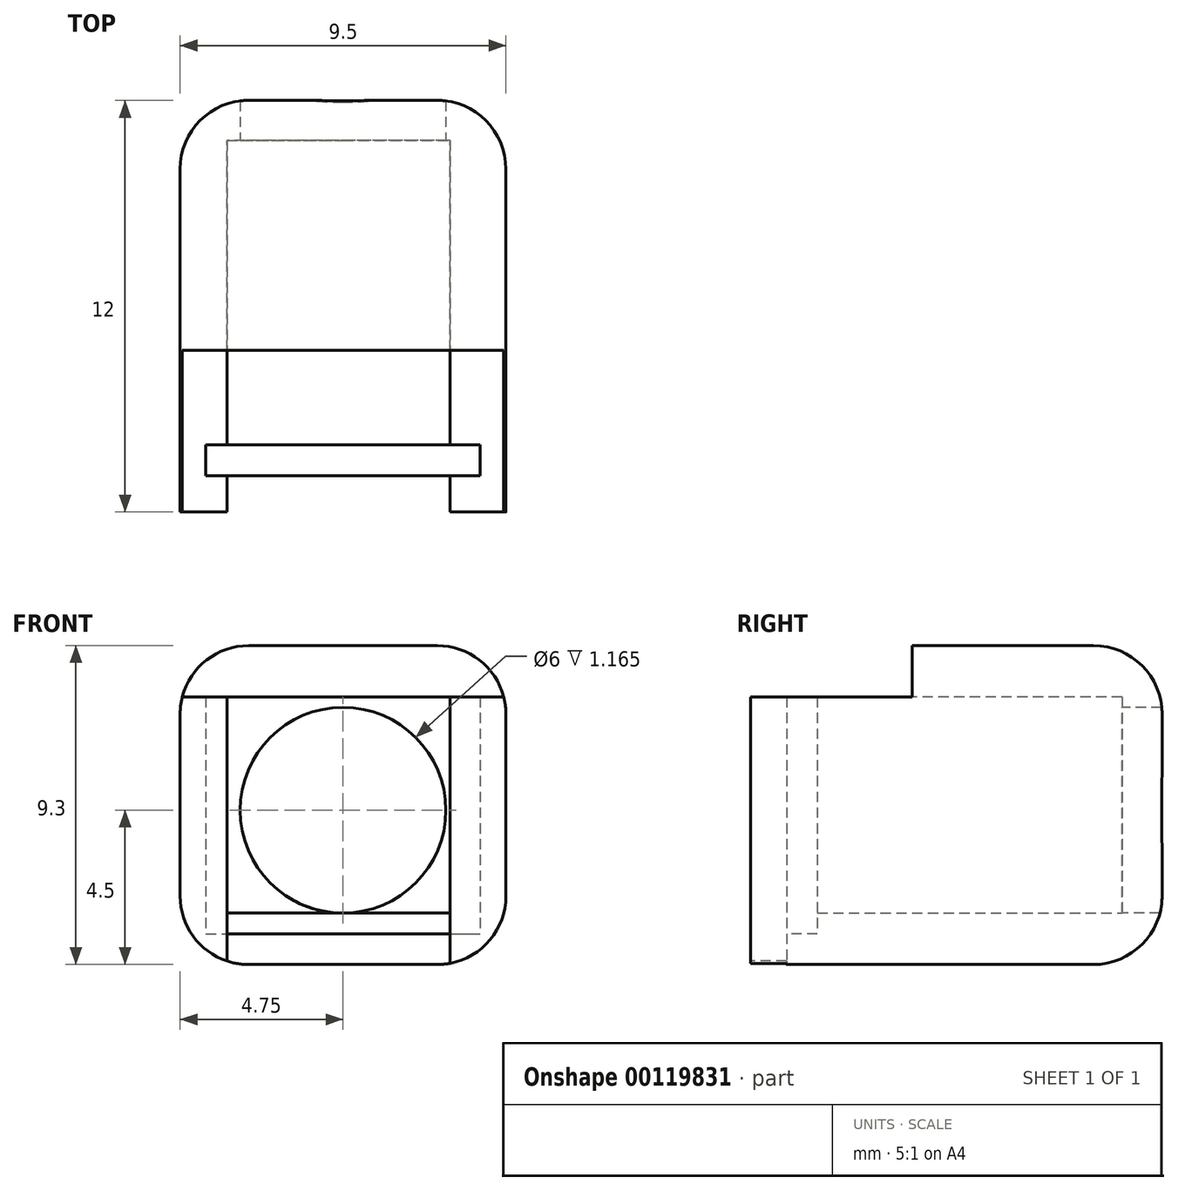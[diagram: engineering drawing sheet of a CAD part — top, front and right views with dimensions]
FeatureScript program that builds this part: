
annotation { "Feature Type Name" : "Feature", "Feature Type Description" : "" }
export const myFeature = defineFeature(function(context is Context, id is Id, definition is map)
    precondition{}
    {
        {
            var Q0;
            Q0=qCreatedBy(makeId("Top.planeOp"),FACE);
            var sketch = newSketch(context, id + "F0", { "sketchPlane" : qUnion([Q0])});
            skPoint(sketch, "E0.rect.middle", {"position": v(0, 0) * mm});
            skLineSegment(sketch, "E1.rect.bottom", {"start": v(-4.75, -1.5) * mm, "end": v(4.75, -1.5) * mm});
            skLineSegment(sketch, "E1.rect.top", {"start": v(-4.75, 1.5) * mm, "end": v(-3.38, 1.5) * mm});
            skLineSegment(sketch, "E1.rect.left", {"start": v(-4.75, -1.5) * mm, "end": v(-4.75, 1.5) * mm});
            skLineSegment(sketch, "E1.rect.right", {"start": v(4.75, -1.5) * mm, "end": v(4.75, 1.5) * mm});
            skLineSegment(sketch, "E2.rect.bottom", {"start": v(4, -0.45) * mm, "end": v(-4, -0.45) * mm});
            skLineSegment(sketch, "E2.rect.top", {"start": v(4, 0.45) * mm, "end": v(-4, 0.45) * mm});
            skLineSegment(sketch, "E2.rect.left", {"start": v(4, -0.45) * mm, "end": v(4, 0.45) * mm});
            skLineSegment(sketch, "E2.rect.right", {"start": v(-4, -0.45) * mm, "end": v(-4, 0.45) * mm});
            skLineSegment(sketch, "E3.rect.bottom", {"start": v(-3.12, -1.5) * mm, "end": v(3.38, -1.5) * mm});
            skLineSegment(sketch, "E4.trimOffspring", {"start": v(3.12, 1.5) * mm, "end": v(4.75, 1.5) * mm});
            skLineSegment(sketch, "E5", {"start": v(-3.38, 1.5) * mm, "end": v(3.12, 1.5) * mm, "construction": true});
            skLineSegment(sketch, "E6.bottom", {"start": v(4.75, 1.5) * mm, "end": v(-4.75, 1.5) * mm});
            skLineSegment(sketch, "E7.bottom", {"start": v(3.12, 1.5) * mm, "end": v(-4.75, 1.5) * mm});
            skLineSegment(sketch, "E8.bottom", {"start": v(-4.75, 1.5) * mm, "end": v(4.75, 1.5) * mm});
            skLineSegment(sketch, "E8.top", {"start": v(-4.75, 10.5) * mm, "end": v(4.75, 10.5) * mm});
            skLineSegment(sketch, "E8.left", {"start": v(-4.75, 1.5) * mm, "end": v(-4.75, 10.5) * mm});
            skLineSegment(sketch, "E8.right", {"start": v(4.75, 1.5) * mm, "end": v(4.75, 10.5) * mm});
            skLineSegment(sketch, "E9", {"start": v(-3.38, 1.5) * mm, "end": v(-3.38, 10.5) * mm});
            skLineSegment(sketch, "E10", {"start": v(3.12, 1.5) * mm, "end": v(3.12, 10.5) * mm});
            skLineSegment(sketch, "E11", {"start": v(4.75, 9.33) * mm, "end": v(-4.75, 9.33) * mm});
            skLineSegment(sketch, "E12", {"start": v(-3.38, 1.5) * mm, "end": v(-3.38, -1.5) * mm});
            skLineSegment(sketch, "E13", {"start": v(3.12, 1.5) * mm, "end": v(3.12, -1.5) * mm});
            skSolve(sketch);
        }
        {
            var Q0;
            {var subQ0=sQuery(id+"F0.wireOp",EDGE,"E6.right");Q0=makeQuery(id+"F0.imprint","IMPRINT",FACE,{"disambiguationData":[TD([[makeQuery(id+"F0.imprint","IMPRINT",EDGE,{"derivedFrom":subQ0}),-1.0]])]});}
            var Q1;
            Q1=makeQuery(id+"F0.imprint","IMPRINT",FACE,{"disambiguationData":[TD([[makeQuery(id+"F0.imprint","IMPRINT",EDGE,{"derivedFrom":sQuery(id+"F0.wireOp",EDGE,"E7.bottom")}),-1.0]])]});
            var Q2;
            {var subQ5=sQuery(id+"F0.wireOp",EDGE,"E7.bottom");Q2=makeQuery(id+"F0.imprint","IMPRINT",FACE,{"disambiguationData":[TD([[makeQuery(id+"F0.imprint","IMPRINT",EDGE,{"derivedFrom":subQ5}),1.0]])]});}
            var Q3;
            {var subQ8=sQuery(id+"F0.wireOp",EDGE,"E1.rect.right");Q3=makeQuery(id+"F0.imprint","IMPRINT",FACE,{"disambiguationData":[TD([[makeQuery(id+"F0.imprint","IMPRINT",EDGE,{"derivedFrom":subQ8}),1.0]])]});}
            var Q4;
            {var subQ5=sQuery(id+"F0.wireOp",EDGE,"E3.rect.bottom");Q4=makeQuery(id+"F0.imprint","IMPRINT",FACE,{"disambiguationData":[TD([[makeQuery(id+"F0.imprint","IMPRINT",EDGE,{"derivedFrom":subQ5}),1.0]])]});}
            var Q5;
            {var subQ4=sQuery(id+"F0.wireOp",EDGE,"E1.rect.left");Q5=makeQuery(id+"F0.imprint","IMPRINT",FACE,{"disambiguationData":[TD([[makeQuery(id+"F0.imprint","IMPRINT",EDGE,{"derivedFrom":subQ4}),-1.0]])]});}
            var Q6;
            {var subQ0=sQuery(id+"F0.wireOp",EDGE,"E6.left");Q6=makeQuery(id+"F0.imprint","IMPRINT",FACE,{"disambiguationData":[TD([[makeQuery(id+"F0.imprint","IMPRINT",EDGE,{"derivedFrom":subQ0}),1.0]])]});}
            var Q7;
            {var subQ0=sQuery(id+"F0.wireOp",EDGE,"E3.rect.right");var subQ1=sQuery(id+"F0.wireOp",EDGE,"E2.rect.bottom");var subQ2=makeQuery(id+"F0.imprint","INTERSECT",VERTEX,{"derivedFrom":[subQ1,subQ0]});Q7=makeQuery(id+"F0.imprint","IMPRINT",FACE,{"disambiguationData":[TD([[makeQuery(id+"F0.imprint","IMPRINT",EDGE,{"disambiguationData":[TD([[subQ2,-1.0]])],"derivedFrom":subQ1}),-1.0]])]});}
            var Q8;
            {var subQ0=sQuery(id+"F0.wireOp",EDGE,"E2.rect.right");Q8=makeQuery(id+"F0.imprint","IMPRINT",FACE,{"disambiguationData":[TD([[makeQuery(id+"F0.imprint","IMPRINT",EDGE,{"derivedFrom":subQ0}),-1.0]])]});}
            var Q9;
            {var subQ0=sQuery(id+"F0.wireOp",EDGE,"E2.rect.left");Q9=makeQuery(id+"F0.imprint","IMPRINT",FACE,{"disambiguationData":[TD([[makeQuery(id+"F0.imprint","IMPRINT",EDGE,{"derivedFrom":subQ0}),1.0]])]});}
            var Q10;
            {var subQ0=sQuery(id+"F0.wireOp",EDGE,"E8.left");var subQ5=sQuery(id+"F0.wireOp",EDGE,"E11");var subQ6=makeQuery(id+"F0.imprint","INTERSECT",VERTEX,{"derivedFrom":[subQ0,subQ5]});Q10=makeQuery(id+"F0.imprint","IMPRINT",FACE,{"disambiguationData":[TD([[makeQuery(id+"F0.imprint","IMPRINT",EDGE,{"disambiguationData":[TD([[subQ6,1.0]])],"derivedFrom":subQ5}),1.0]])]});}
            var Q11;
            {var subQ0=sQuery(id+"F0.wireOp",EDGE,"E8.left");var subQ1=sQuery(id+"F0.wireOp",EDGE,"E8.top");var subQ2=makeQuery(id+"F0.imprint","INTERSECT",VERTEX,{"derivedFrom":[subQ1,subQ0]});Q11=makeQuery(id+"F0.imprint","IMPRINT",FACE,{"disambiguationData":[TD([[makeQuery(id+"F0.imprint","IMPRINT",EDGE,{"disambiguationData":[TD([[subQ2,-1.0]])],"derivedFrom":subQ1}),-1.0]])]});}
            var Q12;
            {var subQ0=sQuery(id+"F0.wireOp",EDGE,"E9");var subQ1=sQuery(id+"F0.wireOp",EDGE,"E8.top");var subQ2=makeQuery(id+"F0.imprint","INTERSECT",VERTEX,{"derivedFrom":[subQ1,subQ0]});Q12=makeQuery(id+"F0.imprint","IMPRINT",FACE,{"disambiguationData":[TD([[makeQuery(id+"F0.imprint","IMPRINT",EDGE,{"disambiguationData":[TD([[subQ2,-1.0]])],"derivedFrom":subQ1}),-1.0]])]});}
            var Q13;
            {var subQ0=sQuery(id+"F0.wireOp",EDGE,"E8.right");var subQ1=sQuery(id+"F0.wireOp",EDGE,"E8.top");var subQ2=makeQuery(id+"F0.imprint","INTERSECT",VERTEX,{"derivedFrom":[subQ1,subQ0]});Q13=makeQuery(id+"F0.imprint","IMPRINT",FACE,{"disambiguationData":[TD([[makeQuery(id+"F0.imprint","IMPRINT",EDGE,{"disambiguationData":[TD([[subQ2,1.0]])],"derivedFrom":subQ1}),-1.0]])]});}
            var Q14;
            {var subQ0=sQuery(id+"F0.wireOp",EDGE,"E8.right");var subQ5=sQuery(id+"F0.wireOp",EDGE,"E11");var subQ6=makeQuery(id+"F0.imprint","INTERSECT",VERTEX,{"derivedFrom":[subQ0,subQ5]});Q14=makeQuery(id+"F0.imprint","IMPRINT",FACE,{"disambiguationData":[TD([[makeQuery(id+"F0.imprint","IMPRINT",EDGE,{"disambiguationData":[TD([[subQ6,-1.0]])],"derivedFrom":subQ5}),1.0]])]});}
            var Q15;
            {var subQ0=sQuery(id+"F0.wireOp",EDGE,"E3.rect.right");var subQ1=sQuery(id+"F0.wireOp",EDGE,"E2.rect.top");var subQ2=makeQuery(id+"F0.imprint","INTERSECT",VERTEX,{"derivedFrom":[subQ1,subQ0]});Q15=makeQuery(id+"F0.imprint","IMPRINT",FACE,{"disambiguationData":[TD([[makeQuery(id+"F0.imprint","IMPRINT",EDGE,{"disambiguationData":[TD([[subQ2,-1.0]])],"derivedFrom":subQ1}),-1.0]])]});}
            var Q16;
            {var subQ0=sQuery(id+"F0.wireOp",EDGE,"E9");var subQ5=sQuery(id+"F0.wireOp",EDGE,"E11");var subQ6=makeQuery(id+"F0.imprint","INTERSECT",VERTEX,{"derivedFrom":[subQ0,subQ5]});Q16=makeQuery(id+"F0.imprint","IMPRINT",FACE,{"disambiguationData":[TD([[makeQuery(id+"F0.imprint","IMPRINT",EDGE,{"disambiguationData":[TD([[subQ6,1.0]])],"derivedFrom":subQ5}),1.0]])]});}
            extrude(context, id + "F1", {"entities" : qUnion([Q0, Q1, Q2, Q3, Q4, Q5, Q6, Q7, Q8, Q9, Q10, Q11, Q12, Q13, Q14, Q15, Q16]), "depth" : 0.9 * mm});
        }
        {
            var Q0;
            {var subQ0=sQuery(id+"F0.wireOp",EDGE,"E6.left");Q0=makeQuery(id+"F0.imprint","IMPRINT",FACE,{"disambiguationData":[TD([[makeQuery(id+"F0.imprint","IMPRINT",EDGE,{"derivedFrom":subQ0}),1.0]])]});}
            var Q1;
            {var subQ0=sQuery(id+"F0.wireOp",EDGE,"E6.right");Q1=makeQuery(id+"F0.imprint","IMPRINT",FACE,{"disambiguationData":[TD([[makeQuery(id+"F0.imprint","IMPRINT",EDGE,{"derivedFrom":subQ0}),-1.0]])]});}
            var Q2;
            {var subQ5=sQuery(id+"F0.wireOp",EDGE,"E3.rect.bottom");Q2=makeQuery(id+"F0.imprint","IMPRINT",FACE,{"disambiguationData":[TD([[makeQuery(id+"F0.imprint","IMPRINT",EDGE,{"derivedFrom":subQ5}),1.0]])]});}
            var Q3;
            {var subQ4=sQuery(id+"F0.wireOp",EDGE,"E1.rect.left");Q3=makeQuery(id+"F0.imprint","IMPRINT",FACE,{"disambiguationData":[TD([[makeQuery(id+"F0.imprint","IMPRINT",EDGE,{"derivedFrom":subQ4}),-1.0]])]});}
            var Q4;
            {var subQ8=sQuery(id+"F0.wireOp",EDGE,"E1.rect.right");Q4=makeQuery(id+"F0.imprint","IMPRINT",FACE,{"disambiguationData":[TD([[makeQuery(id+"F0.imprint","IMPRINT",EDGE,{"derivedFrom":subQ8}),1.0]])]});}
            var Q5;
            {var subQ5=sQuery(id+"F0.wireOp",EDGE,"E7.bottom");Q5=makeQuery(id+"F0.imprint","IMPRINT",FACE,{"disambiguationData":[TD([[makeQuery(id+"F0.imprint","IMPRINT",EDGE,{"derivedFrom":subQ5}),1.0]])]});}
            var Q6;
            {var subQ0=sQuery(id+"F0.wireOp",EDGE,"E8.right");var subQ5=sQuery(id+"F0.wireOp",EDGE,"E11");var subQ6=makeQuery(id+"F0.imprint","INTERSECT",VERTEX,{"derivedFrom":[subQ0,subQ5]});Q6=makeQuery(id+"F0.imprint","IMPRINT",FACE,{"disambiguationData":[TD([[makeQuery(id+"F0.imprint","IMPRINT",EDGE,{"disambiguationData":[TD([[subQ6,-1.0]])],"derivedFrom":subQ5}),1.0]])]});}
            var Q7;
            {var subQ0=sQuery(id+"F0.wireOp",EDGE,"E3.rect.right");var subQ1=sQuery(id+"F0.wireOp",EDGE,"E2.rect.top");var subQ2=makeQuery(id+"F0.imprint","INTERSECT",VERTEX,{"derivedFrom":[subQ1,subQ0]});Q7=makeQuery(id+"F0.imprint","IMPRINT",FACE,{"disambiguationData":[TD([[makeQuery(id+"F0.imprint","IMPRINT",EDGE,{"disambiguationData":[TD([[subQ2,-1.0]])],"derivedFrom":subQ1}),-1.0]])]});}
            var Q8;
            {var subQ0=sQuery(id+"F0.wireOp",EDGE,"E9");var subQ5=sQuery(id+"F0.wireOp",EDGE,"E11");var subQ6=makeQuery(id+"F0.imprint","INTERSECT",VERTEX,{"derivedFrom":[subQ0,subQ5]});Q8=makeQuery(id+"F0.imprint","IMPRINT",FACE,{"disambiguationData":[TD([[makeQuery(id+"F0.imprint","IMPRINT",EDGE,{"disambiguationData":[TD([[subQ6,1.0]])],"derivedFrom":subQ5}),1.0]])]});}
            var Q9;
            {var subQ0=sQuery(id+"F0.wireOp",EDGE,"E8.left");var subQ5=sQuery(id+"F0.wireOp",EDGE,"E11");var subQ6=makeQuery(id+"F0.imprint","INTERSECT",VERTEX,{"derivedFrom":[subQ0,subQ5]});Q9=makeQuery(id+"F0.imprint","IMPRINT",FACE,{"disambiguationData":[TD([[makeQuery(id+"F0.imprint","IMPRINT",EDGE,{"disambiguationData":[TD([[subQ6,1.0]])],"derivedFrom":subQ5}),1.0]])]});}
            var Q10;
            {var subQ0=sQuery(id+"F0.wireOp",EDGE,"E8.left");var subQ1=sQuery(id+"F0.wireOp",EDGE,"E8.top");var subQ2=makeQuery(id+"F0.imprint","INTERSECT",VERTEX,{"derivedFrom":[subQ1,subQ0]});Q10=makeQuery(id+"F0.imprint","IMPRINT",FACE,{"disambiguationData":[TD([[makeQuery(id+"F0.imprint","IMPRINT",EDGE,{"disambiguationData":[TD([[subQ2,-1.0]])],"derivedFrom":subQ1}),-1.0]])]});}
            var Q11;
            {var subQ0=sQuery(id+"F0.wireOp",EDGE,"E9");var subQ1=sQuery(id+"F0.wireOp",EDGE,"E8.top");var subQ2=makeQuery(id+"F0.imprint","INTERSECT",VERTEX,{"derivedFrom":[subQ1,subQ0]});Q11=makeQuery(id+"F0.imprint","IMPRINT",FACE,{"disambiguationData":[TD([[makeQuery(id+"F0.imprint","IMPRINT",EDGE,{"disambiguationData":[TD([[subQ2,-1.0]])],"derivedFrom":subQ1}),-1.0]])]});}
            var Q12;
            {var subQ0=sQuery(id+"F0.wireOp",EDGE,"E8.right");var subQ1=sQuery(id+"F0.wireOp",EDGE,"E8.top");var subQ2=makeQuery(id+"F0.imprint","INTERSECT",VERTEX,{"derivedFrom":[subQ1,subQ0]});Q12=makeQuery(id+"F0.imprint","IMPRINT",FACE,{"disambiguationData":[TD([[makeQuery(id+"F0.imprint","IMPRINT",EDGE,{"disambiguationData":[TD([[subQ2,1.0]])],"derivedFrom":subQ1}),-1.0]])]});}
            extrude(context, id + "F2", {"entities" : qUnion([Q0, Q1, Q2, Q3, Q4, Q5, Q6, Q7, Q8, Q9, Q10, Q11, Q12]), "operationType" : NewBodyOperationType.ADD, "depth" : 1.5 * mm});
        }
        {
            var Q0;
            {var subQ9=sQuery(id+"F0.wireOp",EDGE,"E1.rect.top");Q0=makeQuery(id+"F0.imprint","IMPRINT",FACE,{"disambiguationData":[TD([[makeQuery(id+"F0.imprint","IMPRINT",EDGE,{"derivedFrom":subQ9}),-1.0]])]});}
            var Q1;
            {var subQ4=sQuery(id+"F0.wireOp",EDGE,"E1.rect.right");Q1=makeQuery(id+"F0.imprint","IMPRINT",FACE,{"disambiguationData":[TD([[makeQuery(id+"F0.imprint","IMPRINT",EDGE,{"derivedFrom":subQ4}),1.0]])]});}
            var Q2;
            {var subQ4=sQuery(id+"F0.wireOp",EDGE,"E1.rect.left");Q2=makeQuery(id+"F0.imprint","IMPRINT",FACE,{"disambiguationData":[TD([[makeQuery(id+"F0.imprint","IMPRINT",EDGE,{"derivedFrom":subQ4}),-1.0]])]});}
            var Q3;
            {var subQ0=sQuery(id+"F0.wireOp",EDGE,"E6.right");Q3=makeQuery(id+"F0.imprint","IMPRINT",FACE,{"disambiguationData":[TD([[makeQuery(id+"F0.imprint","IMPRINT",EDGE,{"derivedFrom":subQ0}),-1.0]])]});}
            var Q4;
            {var subQ0=sQuery(id+"F0.wireOp",EDGE,"E6.left");Q4=makeQuery(id+"F0.imprint","IMPRINT",FACE,{"disambiguationData":[TD([[makeQuery(id+"F0.imprint","IMPRINT",EDGE,{"derivedFrom":subQ0}),1.0]])]});}
            var Q5;
            {var subQ0=sQuery(id+"F0.wireOp",EDGE,"E8.left");var subQ5=sQuery(id+"F0.wireOp",EDGE,"E11");var subQ6=makeQuery(id+"F0.imprint","INTERSECT",VERTEX,{"derivedFrom":[subQ0,subQ5]});Q5=makeQuery(id+"F0.imprint","IMPRINT",FACE,{"disambiguationData":[TD([[makeQuery(id+"F0.imprint","IMPRINT",EDGE,{"disambiguationData":[TD([[subQ6,1.0]])],"derivedFrom":subQ5}),1.0]])]});}
            var Q6;
            {var subQ0=sQuery(id+"F0.wireOp",EDGE,"E8.right");var subQ5=sQuery(id+"F0.wireOp",EDGE,"E11");var subQ6=makeQuery(id+"F0.imprint","INTERSECT",VERTEX,{"derivedFrom":[subQ0,subQ5]});Q6=makeQuery(id+"F0.imprint","IMPRINT",FACE,{"disambiguationData":[TD([[makeQuery(id+"F0.imprint","IMPRINT",EDGE,{"disambiguationData":[TD([[subQ6,-1.0]])],"derivedFrom":subQ5}),1.0]])]});}
            var Q7;
            {var subQ0=sQuery(id+"F0.wireOp",EDGE,"E8.left");var subQ1=sQuery(id+"F0.wireOp",EDGE,"E8.top");var subQ2=makeQuery(id+"F0.imprint","INTERSECT",VERTEX,{"derivedFrom":[subQ1,subQ0]});Q7=makeQuery(id+"F0.imprint","IMPRINT",FACE,{"disambiguationData":[TD([[makeQuery(id+"F0.imprint","IMPRINT",EDGE,{"disambiguationData":[TD([[subQ2,-1.0]])],"derivedFrom":subQ1}),-1.0]])]});}
            var Q8;
            {var subQ0=sQuery(id+"F0.wireOp",EDGE,"E9");var subQ1=sQuery(id+"F0.wireOp",EDGE,"E8.top");var subQ2=makeQuery(id+"F0.imprint","INTERSECT",VERTEX,{"derivedFrom":[subQ1,subQ0]});Q8=makeQuery(id+"F0.imprint","IMPRINT",FACE,{"disambiguationData":[TD([[makeQuery(id+"F0.imprint","IMPRINT",EDGE,{"disambiguationData":[TD([[subQ2,-1.0]])],"derivedFrom":subQ1}),-1.0]])]});}
            var Q9;
            {var subQ0=sQuery(id+"F0.wireOp",EDGE,"E8.right");var subQ1=sQuery(id+"F0.wireOp",EDGE,"E8.top");var subQ2=makeQuery(id+"F0.imprint","INTERSECT",VERTEX,{"derivedFrom":[subQ1,subQ0]});Q9=makeQuery(id+"F0.imprint","IMPRINT",FACE,{"disambiguationData":[TD([[makeQuery(id+"F0.imprint","IMPRINT",EDGE,{"disambiguationData":[TD([[subQ2,1.0]])],"derivedFrom":subQ1}),-1.0]])]});}
            extrude(context, id + "F3", {"entities" : qUnion([Q0, Q1, Q2, Q3, Q4, Q5, Q6, Q7, Q8, Q9]), "operationType" : NewBodyOperationType.ADD, "depth" : 7.8 * mm});
        }
        {
            var Q0;
            Q0=makeQuery(id+"F3.opExtrude","CAP_FACE",FACE,{"disambiguationData":[OSD([sQuery(id+"F0.wireOp",EDGE,"E1.rect.bottom"),sQuery(id+"F0.wireOp",EDGE,"E1.rect.left"),sQuery(id+"F0.wireOp",EDGE,"E1.rect.right"),sQuery(id+"F0.wireOp",EDGE,"E2.rect.bottom"),sQuery(id+"F0.wireOp",EDGE,"E2.rect.top"),sQuery(id+"F0.wireOp",EDGE,"E2.rect.left"),sQuery(id+"F0.wireOp",EDGE,"E2.rect.right"),sQuery(id+"F0.wireOp",EDGE,"E3.rect.left"),sQuery(id+"F0.wireOp",EDGE,"E3.rect.right"),sQuery(id+"F0.wireOp",EDGE,"E8.top"),sQuery(id+"F0.wireOp",EDGE,"E8.left"),sQuery(id+"F0.wireOp",EDGE,"E8.right"),sQuery(id+"F0.wireOp",EDGE,"E9"),sQuery(id+"F0.wireOp",EDGE,"E10"),sQuery(id+"F0.wireOp",EDGE,"E11")])],"isStart":false});
            cPlane(context, id + "F4", {"entities" : qUnion([Q0]), "cplaneType" : CPlaneType.OFFSET, "offset" : 0 * mm, "width" : 150 * mm, "height" : 150 * mm});
        }
        {
            var Q0;
            Q0=qCreatedBy(id+"F4.planeOp",FACE);
            var sketch = newSketch(context, id + "F5", { "sketchPlane" : qUnion([Q0])});
            skLineSegment(sketch, "E14.top", {"start": v(4.75, -1.5) * mm, "end": v(-4.75, -1.5) * mm});
            skLineSegment(sketch, "E14.left", {"start": v(4.75, 1.5) * mm, "end": v(4.75, -1.5) * mm});
            skLineSegment(sketch, "E14.right", {"start": v(-4.75, 1.5) * mm, "end": v(-4.75, -1.5) * mm});
            skPoint(sketch, "E14.middle", {"position": v(0, 0) * mm});
            skLineSegment(sketch, "E15.bottom", {"start": v(4.75, 1.5) * mm, "end": v(-4.75, 1.5) * mm});
            skLineSegment(sketch, "E15.top", {"start": v(4.75, 10.5) * mm, "end": v(-4.75, 10.5) * mm});
            skLineSegment(sketch, "E15.left", {"start": v(4.75, 1.5) * mm, "end": v(4.75, 10.5) * mm});
            skLineSegment(sketch, "E15.right", {"start": v(-4.75, 1.5) * mm, "end": v(-4.75, 10.5) * mm});
            skLineSegment(sketch, "E16", {"start": v(4.75, 3.21) * mm, "end": v(-4.75, 3.21) * mm});
            skSolve(sketch);
        }
        {
            var Q0;
            {var subQ0=sQuery(id+"F5.wireOp",EDGE,"E15.top");Q0=makeQuery(id+"F5.imprint","IMPRINT",FACE,{"disambiguationData":[TD([[makeQuery(id+"F5.imprint","IMPRINT",EDGE,{"derivedFrom":subQ0}),1.0]])]});}
            extrude(context, id + "F6", {"entities" : qUnion([Q0]), "operationType" : NewBodyOperationType.ADD, "depth" : 1.5 * mm});
        }
        {
            var Q0;
            Q0=qCreatedBy(makeId("Front.planeOp"),FACE);
            var sketch = newSketch(context, id + "F7", { "sketchPlane" : qUnion([Q0])});
            skLineSegment(sketch, "E17", {"start": v(0, 0) * mm, "end": v(0, 9) * mm, "construction": true});
            skCircle(sketch, "E18", {"center": v(0, 4.5) * mm, "radius": 3 * mm});
            skSolve(sketch);
        }
        {
            var Q0;
            Q0=qSketchRegion(id+"F7",true);
            extrude(context, id + "F8", {"entities" : qUnion([Q0]), "operationType" : NewBodyOperationType.REMOVE, "endBound" : BoundingType.THROUGH_ALL, "oppositeDirection" : true, "depth" : 25 * mm});
        }
        {
            var Q0;
            {var subQ0=sQuery(id+"F0.wireOp",EDGE,"E8.right");var subQ1=sQuery(id+"F0.wireOp",EDGE,"E8.top");Q0=makeQuery(id+"F6.boolean.opBoolean","MERGE",EDGE,{"derivedFrom":[makeQuery(id+"F3.boolean.opBoolean","MERGE",EDGE,{"derivedFrom":[makeQuery(id+"F2.boolean.opBoolean","MERGE",EDGE,{"derivedFrom":[makeQuery(id+"F1.opExtrude","SWEPT_EDGE",EDGE,{"disambiguationData":[OSD([subQ1,subQ0])]}),makeQuery(id+"F2.opExtrude","SWEPT_EDGE",EDGE,{"disambiguationData":[OSD([subQ1,subQ0])]})]}),makeQuery(id+"F3.opExtrude","SWEPT_EDGE",EDGE,{"disambiguationData":[OSD([subQ1,subQ0])]})]}),makeQuery(id+"F6.opExtrude","SWEPT_EDGE",EDGE,{"disambiguationData":[OSD([sQuery(id+"F5.wireOp",EDGE,"E15.top"),sQuery(id+"F5.wireOp",EDGE,"E15.left")])]})]});}
            var Q1;
            Q1=makeQuery(id+"F6.opExtrude","CAP_EDGE",EDGE,{"disambiguationData":[OSD([sQuery(id+"F5.wireOp",EDGE,"E15.top")])],"isStart":false});
            var Q2;
            Q2=makeQuery(id+"F6.opExtrude","CAP_EDGE",EDGE,{"disambiguationData":[OSD([sQuery(id+"F5.wireOp",EDGE,"E15.left")])],"isStart":false});
            var Q3;
            Q3=makeQuery(id+"F1.opExtrude","CAP_EDGE",EDGE,{"disambiguationData":[OSD([sQuery(id+"F0.wireOp",EDGE,"E1.rect.right"),sQuery(id+"F0.wireOp",EDGE,"E8.right")])],"isStart":true});
            var Q4;
            Q4=makeQuery(id+"F1.opExtrude","CAP_EDGE",EDGE,{"disambiguationData":[OSD([sQuery(id+"F0.wireOp",EDGE,"E8.top")])],"isStart":true});
            var Q5;
            Q5=makeQuery(id+"F1.opExtrude","CAP_EDGE",EDGE,{"disambiguationData":[OSD([sQuery(id+"F0.wireOp",EDGE,"E1.rect.left"),sQuery(id+"F0.wireOp",EDGE,"E8.left")])],"isStart":true});
            var Q6;
            {var subQ0=sQuery(id+"F0.wireOp",EDGE,"E8.left");var subQ1=sQuery(id+"F0.wireOp",EDGE,"E8.top");Q6=makeQuery(id+"F6.boolean.opBoolean","MERGE",EDGE,{"derivedFrom":[makeQuery(id+"F3.boolean.opBoolean","MERGE",EDGE,{"derivedFrom":[makeQuery(id+"F2.boolean.opBoolean","MERGE",EDGE,{"derivedFrom":[makeQuery(id+"F1.opExtrude","SWEPT_EDGE",EDGE,{"disambiguationData":[OSD([subQ1,subQ0])]}),makeQuery(id+"F2.opExtrude","SWEPT_EDGE",EDGE,{"disambiguationData":[OSD([subQ1,subQ0])]})]}),makeQuery(id+"F3.opExtrude","SWEPT_EDGE",EDGE,{"disambiguationData":[OSD([subQ1,subQ0])]})]}),makeQuery(id+"F6.opExtrude","SWEPT_EDGE",EDGE,{"disambiguationData":[OSD([sQuery(id+"F5.wireOp",EDGE,"E15.top"),sQuery(id+"F5.wireOp",EDGE,"E15.right")])]})]});}
            var Q7;
            Q7=makeQuery(id+"F6.opExtrude","CAP_EDGE",EDGE,{"disambiguationData":[OSD([sQuery(id+"F5.wireOp",EDGE,"E15.right")])],"isStart":false});
            fillet(context, id + "F9", {"entities" : qUnion([Q0, Q1, Q2, Q3, Q4, Q5, Q6, Q7]), "radius" : 2 * mm, "tangentPropagation" : true, "allowEdgeOverflow" : false});
        }
    });
